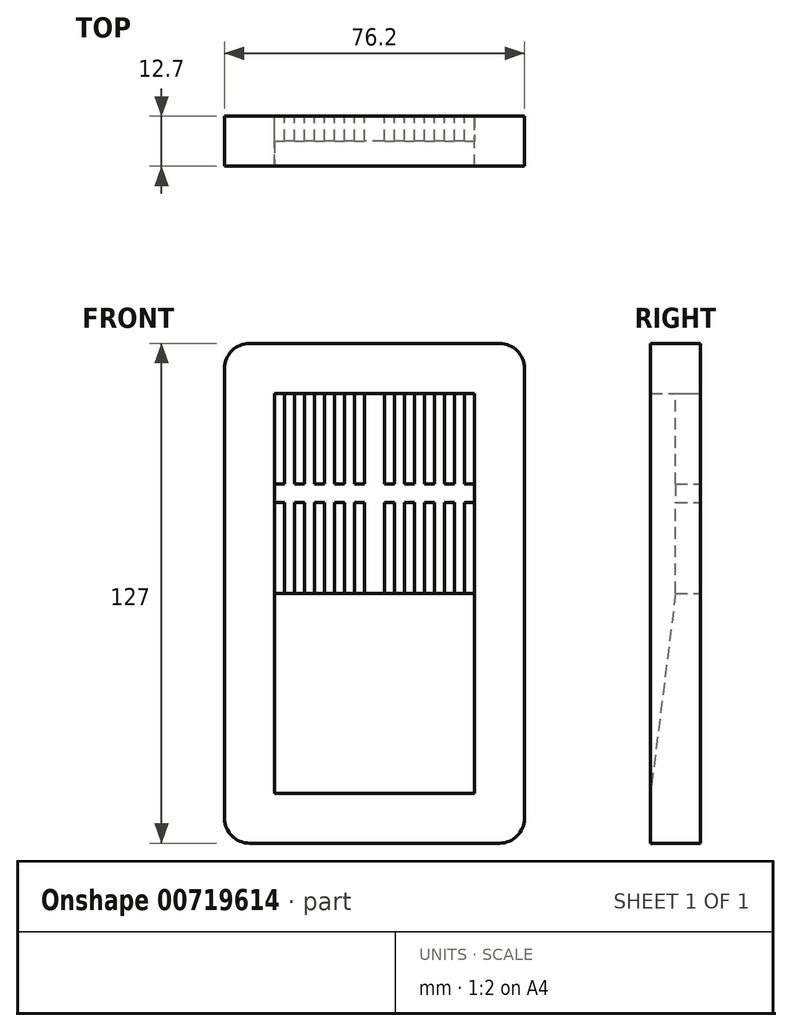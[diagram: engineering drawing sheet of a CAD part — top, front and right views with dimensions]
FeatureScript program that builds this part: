
annotation { "Feature Type Name" : "Feature", "Feature Type Description" : "" }
export const myFeature = defineFeature(function(context is Context, id is Id, definition is map)
    precondition{}
    {
        {
            var Q0;
            Q0=qCreatedBy(makeId("Front.planeOp"),FACE);
            var sketch = newSketch(context, id + "F0", { "sketchPlane" : qUnion([Q0])});
            skLineSegment(sketch, "E0.bottom", {"start": v(31.75, 63.5) * mm, "end": v(-31.75, 63.5) * mm});
            skLineSegment(sketch, "E0.top", {"start": v(31.75, -63.5) * mm, "end": v(-31.75, -63.5) * mm});
            skLineSegment(sketch, "E0.left", {"start": v(38.1, 57.15) * mm, "end": v(38.1, -57.15) * mm});
            skLineSegment(sketch, "E0.right", {"start": v(-38.1, 57.15) * mm, "end": v(-38.1, -57.15) * mm});
            skPoint(sketch, "E0.middle", {"position": v(0, 0) * mm});
            skPoint(sketch, "E1.visualSharp", {"position": v(-38.1, 63.5) * mm});
            skArc(sketch, "E1.filletArc", {"start": v(-31.75, 63.5) * mm, "mid": v(-36.24, 61.64) * mm, "end": v(-38.1, 57.15) * mm});
            skPoint(sketch, "E2.visualSharp", {"position": v(38.1, 63.5) * mm});
            skArc(sketch, "E2.filletArc", {"start": v(38.1, 57.15) * mm, "mid": v(36.24, 61.64) * mm, "end": v(31.75, 63.5) * mm});
            skPoint(sketch, "E3.visualSharp", {"position": v(-38.1, -63.5) * mm});
            skArc(sketch, "E3.filletArc", {"start": v(-38.1, -57.15) * mm, "mid": v(-36.24, -61.64) * mm, "end": v(-31.75, -63.5) * mm});
            skPoint(sketch, "E4.visualSharp", {"position": v(38.1, -63.5) * mm});
            skArc(sketch, "E4.filletArc", {"start": v(31.75, -63.5) * mm, "mid": v(36.24, -61.64) * mm, "end": v(38.1, -57.15) * mm});
            skLineSegment(sketch, "E5.bottom", {"start": v(25.4, 50.8) * mm, "end": v(-25.4, 50.8) * mm});
            skLineSegment(sketch, "E5.top", {"start": v(25.4, -50.8) * mm, "end": v(-25.4, -50.8) * mm});
            skLineSegment(sketch, "E5.left", {"start": v(25.4, 50.8) * mm, "end": v(25.4, -50.8) * mm});
            skLineSegment(sketch, "E5.right", {"start": v(-25.4, 50.8) * mm, "end": v(-25.4, -50.8) * mm});
            skLineSegment(sketch, "E6", {"start": v(-25.4, 0) * mm, "end": v(25.4, 0) * mm});
            skLineSegment(sketch, "E7.bottom", {"start": v(-25.4, 0) * mm, "end": v(-22.86, 0) * mm});
            skLineSegment(sketch, "E7.top", {"start": v(-25.4, 50.8) * mm, "end": v(-22.86, 50.8) * mm});
            skLineSegment(sketch, "E7.left", {"start": v(-25.4, 0) * mm, "end": v(-25.4, 23.04) * mm});
            skLineSegment(sketch, "E7.right", {"start": v(-22.86, 0) * mm, "end": v(-22.86, 23.04) * mm});
            skLineSegment(sketch, "E8.bottom", {"start": v(-22.86, 0) * mm, "end": v(-20.32, 0) * mm});
            skLineSegment(sketch, "E8.top", {"start": v(-22.86, 50.8) * mm, "end": v(-20.32, 50.8) * mm});
            skLineSegment(sketch, "E8.right", {"start": v(-20.32, 0) * mm, "end": v(-20.32, 23.04) * mm});
            skLineSegment(sketch, "E9.bottom", {"start": v(-20.32, 0) * mm, "end": v(-17.78, 0) * mm});
            skLineSegment(sketch, "E9.top", {"start": v(-20.32, 50.8) * mm, "end": v(-17.78, 50.8) * mm});
            skLineSegment(sketch, "E9.right", {"start": v(-17.78, 0) * mm, "end": v(-17.78, 23.04) * mm});
            skLineSegment(sketch, "E10.bottom", {"start": v(-17.78, 0) * mm, "end": v(-15.24, 0) * mm});
            skLineSegment(sketch, "E10.top", {"start": v(-17.78, 50.8) * mm, "end": v(-15.24, 50.8) * mm});
            skLineSegment(sketch, "E10.right", {"start": v(-15.24, 0) * mm, "end": v(-15.24, 23.04) * mm});
            skLineSegment(sketch, "E11.bottom", {"start": v(-15.24, 0) * mm, "end": v(-12.7, 0) * mm});
            skLineSegment(sketch, "E11.top", {"start": v(-15.24, 50.8) * mm, "end": v(-12.7, 50.8) * mm});
            skLineSegment(sketch, "E11.right", {"start": v(-12.7, 0) * mm, "end": v(-12.7, 23.04) * mm});
            skLineSegment(sketch, "E12.bottom", {"start": v(-12.7, 0) * mm, "end": v(-10.16, 0) * mm});
            skLineSegment(sketch, "E12.top", {"start": v(-12.7, 50.8) * mm, "end": v(-10.16, 50.8) * mm});
            skLineSegment(sketch, "E12.right", {"start": v(-10.16, 0) * mm, "end": v(-10.16, 23.04) * mm});
            skLineSegment(sketch, "E13.bottom", {"start": v(-10.16, 0) * mm, "end": v(-7.62, 0) * mm});
            skLineSegment(sketch, "E13.top", {"start": v(-10.16, 50.8) * mm, "end": v(-7.62, 50.8) * mm});
            skLineSegment(sketch, "E13.right", {"start": v(-7.62, 0) * mm, "end": v(-7.62, 23.04) * mm});
            skLineSegment(sketch, "E14.bottom", {"start": v(-7.62, 0) * mm, "end": v(-5.08, 0) * mm});
            skLineSegment(sketch, "E14.top", {"start": v(-7.62, 50.8) * mm, "end": v(-5.08, 50.8) * mm});
            skLineSegment(sketch, "E14.right", {"start": v(-5.08, 0) * mm, "end": v(-5.08, 23.04) * mm});
            skLineSegment(sketch, "E15.bottom", {"start": v(-5.08, 0) * mm, "end": v(-2.54, 0) * mm});
            skLineSegment(sketch, "E15.top", {"start": v(-5.08, 50.8) * mm, "end": v(-2.54, 50.8) * mm});
            skLineSegment(sketch, "E15.right", {"start": v(-2.54, 0) * mm, "end": v(-2.54, 23.04) * mm});
            skLineSegment(sketch, "E16.bottom", {"start": v(-2.54, 0) * mm, "end": v(0, 0) * mm});
            skLineSegment(sketch, "E16.top", {"start": v(-2.54, 50.8) * mm, "end": v(0, 50.8) * mm});
            skLineSegment(sketch, "E17.bottom", {"start": v(25.4, 0) * mm, "end": v(22.86, 0) * mm});
            skLineSegment(sketch, "E17.top", {"start": v(25.4, 50.8) * mm, "end": v(22.86, 50.8) * mm});
            skLineSegment(sketch, "E17.left", {"start": v(25.4, 0) * mm, "end": v(25.4, 27.76) * mm});
            skLineSegment(sketch, "E17.right", {"start": v(22.86, 0) * mm, "end": v(22.86, 23.04) * mm});
            skLineSegment(sketch, "E18.bottom", {"start": v(22.86, 0) * mm, "end": v(20.32, 0) * mm});
            skLineSegment(sketch, "E18.top", {"start": v(22.86, 50.8) * mm, "end": v(20.32, 50.8) * mm});
            skLineSegment(sketch, "E18.right", {"start": v(20.32, 0) * mm, "end": v(20.32, 23.04) * mm});
            skLineSegment(sketch, "E19.bottom", {"start": v(20.32, 0) * mm, "end": v(17.78, 0) * mm});
            skLineSegment(sketch, "E19.top", {"start": v(20.32, 50.8) * mm, "end": v(17.78, 50.8) * mm});
            skLineSegment(sketch, "E19.right", {"start": v(17.78, 0) * mm, "end": v(17.78, 23.04) * mm});
            skLineSegment(sketch, "E20.bottom", {"start": v(17.78, 0) * mm, "end": v(15.24, 0) * mm});
            skLineSegment(sketch, "E20.top", {"start": v(17.78, 50.8) * mm, "end": v(15.24, 50.8) * mm});
            skLineSegment(sketch, "E20.right", {"start": v(15.24, 0) * mm, "end": v(15.24, 23.04) * mm});
            skLineSegment(sketch, "E21.bottom", {"start": v(15.24, 0) * mm, "end": v(12.7, 0) * mm});
            skLineSegment(sketch, "E21.top", {"start": v(15.24, 50.8) * mm, "end": v(12.7, 50.8) * mm});
            skLineSegment(sketch, "E21.right", {"start": v(12.7, 0) * mm, "end": v(12.7, 23.04) * mm});
            skLineSegment(sketch, "E22.bottom", {"start": v(12.7, 0) * mm, "end": v(10.16, 0) * mm});
            skLineSegment(sketch, "E22.top", {"start": v(12.7, 50.8) * mm, "end": v(10.16, 50.8) * mm});
            skLineSegment(sketch, "E22.right", {"start": v(10.16, 0) * mm, "end": v(10.16, 23.04) * mm});
            skLineSegment(sketch, "E23.bottom", {"start": v(10.16, 0) * mm, "end": v(7.62, 0) * mm});
            skLineSegment(sketch, "E23.top", {"start": v(10.16, 50.8) * mm, "end": v(7.62, 50.8) * mm});
            skLineSegment(sketch, "E23.right", {"start": v(7.62, 0) * mm, "end": v(7.62, 23.04) * mm});
            skLineSegment(sketch, "E24.bottom", {"start": v(7.62, 0) * mm, "end": v(5.08, 0) * mm});
            skLineSegment(sketch, "E24.top", {"start": v(7.62, 50.8) * mm, "end": v(5.08, 50.8) * mm});
            skLineSegment(sketch, "E24.right", {"start": v(5.08, 0) * mm, "end": v(5.08, 23.04) * mm});
            skLineSegment(sketch, "E25.bottom", {"start": v(5.08, 0) * mm, "end": v(2.54, 0) * mm});
            skLineSegment(sketch, "E25.top", {"start": v(5.08, 50.8) * mm, "end": v(2.54, 50.8) * mm});
            skLineSegment(sketch, "E25.right", {"start": v(2.54, 0) * mm, "end": v(2.54, 23.04) * mm});
            skPoint(sketch, "E26", {"position": v(25.4, 0) * mm});
            skPoint(sketch, "E27", {"position": v(25.4, 25.4) * mm});
            skLineSegment(sketch, "E28.top", {"start": v(25.4, 23.04) * mm, "end": v(22.86, 23.04) * mm});
            skLineSegment(sketch, "E28.left", {"start": v(25.4, 27.76) * mm, "end": v(25.4, 23.04) * mm});
            skLineSegment(sketch, "E28.right", {"start": v(-25.4, 27.76) * mm, "end": v(-25.4, 23.04) * mm});
            skPoint(sketch, "E28.middle", {"position": v(0, 25.4) * mm});
            skLineSegment(sketch, "E29", {"start": v(-22.86, 27.76) * mm, "end": v(-22.86, 50.8) * mm});
            skLineSegment(sketch, "E30", {"start": v(-20.32, 27.76) * mm, "end": v(-20.32, 50.8) * mm});
            skLineSegment(sketch, "E31", {"start": v(-17.78, 27.76) * mm, "end": v(-17.78, 50.8) * mm});
            skLineSegment(sketch, "E32", {"start": v(-15.24, 27.76) * mm, "end": v(-15.24, 50.8) * mm});
            skLineSegment(sketch, "E33", {"start": v(-12.7, 27.76) * mm, "end": v(-12.7, 50.8) * mm});
            skLineSegment(sketch, "E34", {"start": v(-10.16, 27.76) * mm, "end": v(-10.16, 50.8) * mm});
            skLineSegment(sketch, "E35", {"start": v(-7.62, 27.76) * mm, "end": v(-7.62, 50.8) * mm});
            skLineSegment(sketch, "E36", {"start": v(-5.08, 27.76) * mm, "end": v(-5.08, 27.76) * mm});
            skLineSegment(sketch, "E37", {"start": v(-2.54, 27.76) * mm, "end": v(-2.54, 50.8) * mm});
            skLineSegment(sketch, "E38", {"start": v(2.54, 27.76) * mm, "end": v(2.54, 50.8) * mm});
            skLineSegment(sketch, "E39", {"start": v(5.08, 27.76) * mm, "end": v(5.08, 50.8) * mm});
            skLineSegment(sketch, "E40", {"start": v(7.62, 27.76) * mm, "end": v(7.62, 50.8) * mm});
            skLineSegment(sketch, "E41", {"start": v(10.16, 27.76) * mm, "end": v(10.16, 50.8) * mm});
            skLineSegment(sketch, "E42", {"start": v(12.7, 27.76) * mm, "end": v(12.7, 50.8) * mm});
            skLineSegment(sketch, "E43", {"start": v(15.24, 27.76) * mm, "end": v(15.24, 50.8) * mm});
            skLineSegment(sketch, "E44", {"start": v(17.78, 27.76) * mm, "end": v(17.78, 50.8) * mm});
            skLineSegment(sketch, "E45", {"start": v(20.32, 27.76) * mm, "end": v(20.32, 50.8) * mm});
            skLineSegment(sketch, "E46", {"start": v(22.86, 27.76) * mm, "end": v(22.86, 50.8) * mm});
            skLineSegment(sketch, "E47", {"start": v(25.4, 27.76) * mm, "end": v(25.4, 50.8) * mm});
            skLineSegment(sketch, "E48", {"start": v(-25.4, 27.76) * mm, "end": v(-25.4, 50.8) * mm});
            skLineSegment(sketch, "E49", {"start": v(-25.4, 23.04) * mm, "end": v(-25.4, 27.76) * mm});
            skLineSegment(sketch, "E50", {"start": v(-12.7, 23.04) * mm, "end": v(-15.24, 23.04) * mm});
            skLineSegment(sketch, "E51", {"start": v(-7.62, 23.04) * mm, "end": v(-10.16, 23.04) * mm});
            skLineSegment(sketch, "E52", {"start": v(-5.08, 23.04) * mm, "end": v(-5.08, 23.04) * mm});
            skLineSegment(sketch, "E53", {"start": v(-2.54, 23.04) * mm, "end": v(-5.08, 23.04) * mm});
            skLineSegment(sketch, "E54", {"start": v(5.08, 23.04) * mm, "end": v(2.54, 23.04) * mm});
            skLineSegment(sketch, "E55", {"start": v(10.16, 23.04) * mm, "end": v(7.62, 23.04) * mm});
            skLineSegment(sketch, "E56", {"start": v(15.24, 23.04) * mm, "end": v(12.7, 23.04) * mm});
            skLineSegment(sketch, "E57", {"start": v(20.32, 23.04) * mm, "end": v(17.78, 23.04) * mm});
            skLineSegment(sketch, "E58", {"start": v(-22.86, 23.04) * mm, "end": v(-25.4, 23.04) * mm});
            skLineSegment(sketch, "E59", {"start": v(-25.4, 23.04) * mm, "end": v(-25.4, 23.04) * mm});
            skLineSegment(sketch, "E60", {"start": v(-5.08, 27.76) * mm, "end": v(-5.08, 50.8) * mm});
            skLineSegment(sketch, "E61", {"start": v(-25.4, 27.76) * mm, "end": v(-22.86, 27.76) * mm});
            skLineSegment(sketch, "E62", {"start": v(-20.32, 27.76) * mm, "end": v(-17.78, 27.76) * mm});
            skLineSegment(sketch, "E63", {"start": v(-15.24, 27.76) * mm, "end": v(-12.7, 27.76) * mm});
            skLineSegment(sketch, "E64", {"start": v(-10.16, 27.76) * mm, "end": v(-7.62, 27.76) * mm});
            skLineSegment(sketch, "E65", {"start": v(-5.08, 27.76) * mm, "end": v(-2.54, 27.76) * mm});
            skLineSegment(sketch, "E66", {"start": v(2.54, 27.76) * mm, "end": v(5.08, 27.76) * mm});
            skLineSegment(sketch, "E67", {"start": v(7.62, 27.76) * mm, "end": v(10.16, 27.76) * mm});
            skLineSegment(sketch, "E68", {"start": v(12.7, 27.76) * mm, "end": v(15.24, 27.76) * mm});
            skLineSegment(sketch, "E69", {"start": v(17.78, 27.76) * mm, "end": v(20.32, 27.76) * mm});
            skLineSegment(sketch, "E70", {"start": v(22.86, 27.76) * mm, "end": v(25.4, 27.76) * mm});
            skLineSegment(sketch, "E71", {"start": v(-17.78, 23.04) * mm, "end": v(-20.32, 23.04) * mm});
            skSolve(sketch);
        }
        {
            var Q0;
            Q0=makeQuery(id+"F0.imprint","IMPRINT",FACE,{"disambiguationData":[TD([[makeQuery(id+"F0.imprint","IMPRINT",EDGE,{"derivedFrom":sQuery(id+"F0.wireOp",EDGE,"E0.bottom")}),1.0]])]});
            extrude(context, id + "F1", {"entities" : qUnion([Q0]), "depth" : 12.7 * mm, "offsetDistance" : 25.4 * mm});
        }
        {
            var Q0;
            Q0=makeQuery(id+"F0.imprint","IMPRINT",FACE,{"disambiguationData":[TD([[makeQuery(id+"F0.imprint","IMPRINT",EDGE,{"derivedFrom":sQuery(id+"F0.wireOp",EDGE,"E5.bottom")}),1.0]])]});
            extrude(context, id + "F2", {"entities" : qUnion([Q0]), "operationType" : NewBodyOperationType.ADD, "depth" : 6.35 * mm, "offsetDistance" : 25.4 * mm});
        }
        {
            var Q0;
            Q0=qCreatedBy(makeId("Right.planeOp"),FACE);
            var sketch = newSketch(context, id + "F3", { "sketchPlane" : qUnion([Q0])});
            skLineSegment(sketch, "E72", {"start": v(0, 0) * mm, "end": v(-6.35, 0) * mm});
            skLineSegment(sketch, "E73", {"start": v(0, 0) * mm, "end": v(0, -50.8) * mm});
            skLineSegment(sketch, "E74", {"start": v(0, -50.8) * mm, "end": v(-12.7, -50.8) * mm});
            skLineSegment(sketch, "E75", {"start": v(-12.7, -50.8) * mm, "end": v(-6.35, 0) * mm});
            skSolve(sketch);
        }
        {
            var Q0;
            Q0=makeQuery(id+"F3.imprint","IMPRINT",FACE,{"disambiguationData":[TD([[makeQuery(id+"F3.imprint","IMPRINT",EDGE,{"derivedFrom":sQuery(id+"F3.wireOp",EDGE,"E72")}),1.0]])]});
            extrude(context, id + "F4", {"entities" : qUnion([Q0]), "operationType" : NewBodyOperationType.ADD, "endBound" : BoundingType.UP_TO_NEXT, "depth" : 25.4 * mm, "offsetDistance" : 25.4 * mm});
        }
        {
            var Q0;
            Q0=makeQuery(id+"F4.opExtrude","CAP_FACE",FACE,{"disambiguationData":[OSD([sQuery(id+"F3.wireOp",EDGE,"E72"),sQuery(id+"F3.wireOp",EDGE,"E73"),sQuery(id+"F3.wireOp",EDGE,"E74"),sQuery(id+"F3.wireOp",EDGE,"E75")])],"isStart":true});
            extrude(context, id + "F5", {"entities" : qUnion([Q0]), "operationType" : NewBodyOperationType.ADD, "endBound" : BoundingType.UP_TO_NEXT, "depth" : 25.4 * mm, "offsetDistance" : 25.4 * mm});
        }
    });
